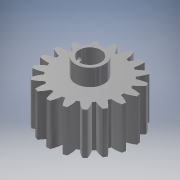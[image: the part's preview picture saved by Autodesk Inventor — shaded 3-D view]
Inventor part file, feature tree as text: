
AUTODESK INVENTOR PART (.ipt)
format: ipt  version: 2018 (Build 220112000, 112)  size: 296,960 bytes
history: native  units: mm (DEFAULTED — no unit token found)
features: other x7, sketch x5, extrude x4, plane x4, projected_geometry x2
ambient origin geometry x8: Origin, YZ Plane, XZ Plane, XY Plane, X Axis, Y Axis, Z Axis, Center Point
bodies: Body1 (feature_tree), Body2 (feature_tree)
feature tree (22):
  other  "Table"
  other  "Engranaje recto11-01"
  other  "Engranaje recto11-02"
  extrude  "Extrusion1"  Depth=30.0mm TaperAngle=0.0deg
  plane  "Work Plane2"
  plane  "Work Plane8"
  plane  "Work Plane9"
  other  "Engranaje recto"
  extrude  "Extrusión2"  Depth=10.0mm TaperAngle=0.0deg
  extrude  "Extrusión3"  Depth=1.745329mm TaperAngle=0.0deg
  plane  "Plano de trabajo11"
  extrude  "Extrusión4"  TaperAngle=0.0deg  [1 undecoded]
  sketch  "Sketch1"  dims[d0=60.0mm d1=30.0mm d2=0.0mm]
  sketch  "Sketch2"  dims[d3=54.0mm d4=10.0mm d5=0.0mm]
  other  "Srf1"
  sketch  "Boceto3"  dims[d16=108.0mm d17=0.0mm d34=1.745329mm]
  sketch  "Boceto4"  dims[d39=0.0mm d41=0.0mm]
  projected_geometry  "Contorno proyectado1"
  sketch  "Boceto5"  dims[d43=108.0mm d46=108.0mm d47=0.0mm d48=0.0mm d49=15.5mm d50=10.0mm d51=0.0mm d52=2.5mm d53=12.0mm d54=0.0mm d55=-12.75mm d56=3.5mm d57=6.2mm d58=0.0mm]
  projected_geometry  "Contorno proyectado2"
  other  "Engranaje recto1"
  other  "Diámetro de separación"
note: 1 required parameter value undecoded (feature->parameter linkage not recoverable at this tier; creation-order binding heuristic only, values carry confidence <= 0.55)
